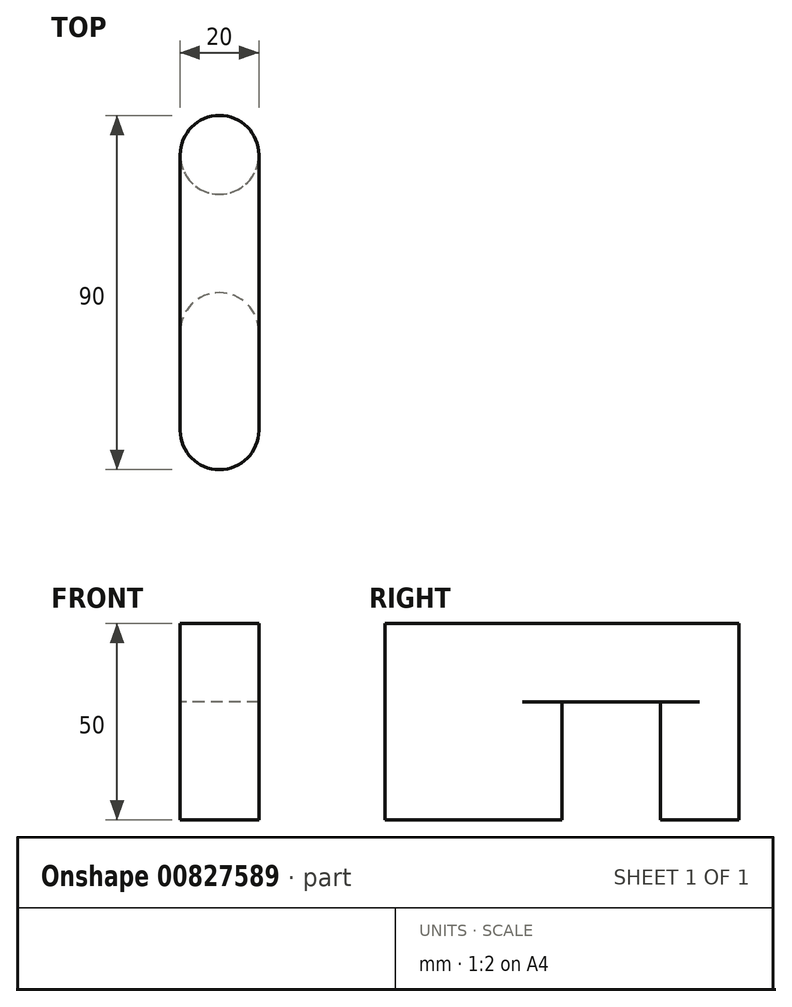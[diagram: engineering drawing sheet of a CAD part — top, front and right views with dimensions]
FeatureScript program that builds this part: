
annotation { "Feature Type Name" : "Feature", "Feature Type Description" : "" }
export const myFeature = defineFeature(function(context is Context, id is Id, definition is map)
    precondition{}
    {
        {
            var Q0;
            Q0=qCreatedBy(makeId("Top.planeOp"),FACE);
            var sketch = newSketch(context, id + "F0", { "sketchPlane" : qUnion([Q0])});
            skCircle(sketch, "E0", {"center": v(0, 0) * mm, "radius": 10 * mm});
            skSolve(sketch);
        }
        {
            var Q0;
            Q0 = qSketchRegion(id + "F0", true);
            extrude(context, id + "F1", {"entities" : qUnion([Q0]), "depth" : 50 * mm, "offsetDistance" : 25 * mm});
        }
        {
            var Q0;
            Q0=makeQuery(id+"F1.opExtrude","CAP_FACE",FACE,{"disambiguationData":[OSD([sQuery(id+"F0.wireOp",EDGE,"E0")])],"isStart":false});
            var sketch = newSketch(context, id + "F2", { "sketchPlane" : qUnion([Q0])});
            skLineSegment(sketch, "E1.bottom", {"start": v(-10, 0) * mm, "end": v(10, 0) * mm});
            skLineSegment(sketch, "E1.top", {"start": v(-10, -70) * mm, "end": v(10, -70) * mm});
            skLineSegment(sketch, "E1.left", {"start": v(-10, 0) * mm, "end": v(-10, -70) * mm});
            skLineSegment(sketch, "E1.right", {"start": v(10, 0) * mm, "end": v(10, -70) * mm});
            skSolve(sketch);
        }
        {
            var Q0;
            Q0=makeQuery(id+"F2.imprint","IMPRINT",FACE,{"disambiguationData":[TD([[makeQuery(id+"F2.imprint","IMPRINT",EDGE,{"derivedFrom":sQuery(id+"F2.wireOp",EDGE,"E1.top")}),1.0]])]});
            extrude(context, id + "F3", {"entities" : qUnion([Q0]), "operationType" : NewBodyOperationType.ADD, "oppositeDirection" : true, "depth" : 20 * mm, "offsetDistance" : 25 * mm});
        }
        {
            var Q0;
            {var subQ0=sQuery(id+"F0.wireOp",EDGE,"E0");Q0=makeQuery(id+"F3.boolean.opBoolean","MERGE",FACE,{"derivedFrom":[makeQuery(id+"F1.opExtrude","CAP_FACE",FACE,{"disambiguationData":[OSD([subQ0])],"isStart":false}),makeQuery(id+"F3.opExtrude","CAP_FACE",FACE,{"disambiguationData":[OSD([subQ0,sQuery(id+"F2.wireOp",EDGE,"E1.top"),sQuery(id+"F2.wireOp",EDGE,"E1.left"),sQuery(id+"F2.wireOp",EDGE,"E1.right")])],"isStart":true})]});}
            var sketch = newSketch(context, id + "F4", { "sketchPlane" : qUnion([Q0])});
            skLineSegment(sketch, "E2.bottom", {"start": v(-10, -70) * mm, "end": v(10, -70) * mm});
            skLineSegment(sketch, "E2.top", {"start": v(-10, -35) * mm, "end": v(10, -35) * mm});
            skLineSegment(sketch, "E2.left", {"start": v(-10, -35) * mm, "end": v(-10, -70) * mm});
            skLineSegment(sketch, "E2.right", {"start": v(10, -35) * mm, "end": v(10, -70) * mm});
            skCircle(sketch, "E3", {"center": v(0, -70) * mm, "radius": 10 * mm});
            skSolve(sketch);
        }
        {
            var Q0;
            Q0=makeQuery(id+"F4.imprint","IMPRINT",FACE,{"disambiguationData":[TD([[makeQuery(id+"F4.imprint","IMPRINT",EDGE,{"derivedFrom":sQuery(id+"F4.wireOp",EDGE,"E2.top")}),-1.0]])]});
            var Q1;
            {var subQ0=sQuery(id+"F4.wireOp",EDGE,"E2.bottom");Q1=makeQuery(id+"F4.imprint","IMPRINT",FACE,{"disambiguationData":[TD([[makeQuery(id+"F4.imprint","IMPRINT",EDGE,{"derivedFrom":subQ0}),1.0]])]});}
            var Q2;
            {var subQ0=sQuery(id+"F4.wireOp",EDGE,"E2.bottom");Q2=makeQuery(id+"F4.imprint","IMPRINT",FACE,{"disambiguationData":[TD([[makeQuery(id+"F4.imprint","IMPRINT",EDGE,{"derivedFrom":subQ0}),-1.0]])]});}
            extrude(context, id + "F5", {"entities" : qUnion([Q0, Q1, Q2]), "operationType" : NewBodyOperationType.ADD, "oppositeDirection" : true, "depth" : 50 * mm, "offsetDistance" : 25 * mm});
        }
        {
            var Q0;
            Q0=makeQuery(id+"F5.opExtrude","SWEPT_EDGE",EDGE,{"disambiguationData":[OSD([sQuery(id+"F2.wireOp",EDGE,"E1.right"),sQuery(id+"F4.wireOp",EDGE,"E2.top"),sQuery(id+"F4.wireOp",EDGE,"E2.right")])]});
            var Q1;
            Q1=makeQuery(id+"F5.opExtrude","SWEPT_EDGE",EDGE,{"disambiguationData":[OSD([sQuery(id+"F2.wireOp",EDGE,"E1.left"),sQuery(id+"F4.wireOp",EDGE,"E2.top"),sQuery(id+"F4.wireOp",EDGE,"E2.left")])]});
            fillet(context, id + "F6", {"entities" : qUnion([Q0, Q1]), "radius" : 10 * mm, "tangentPropagation" : true, "allowEdgeOverflow" : false});
        }
    });
